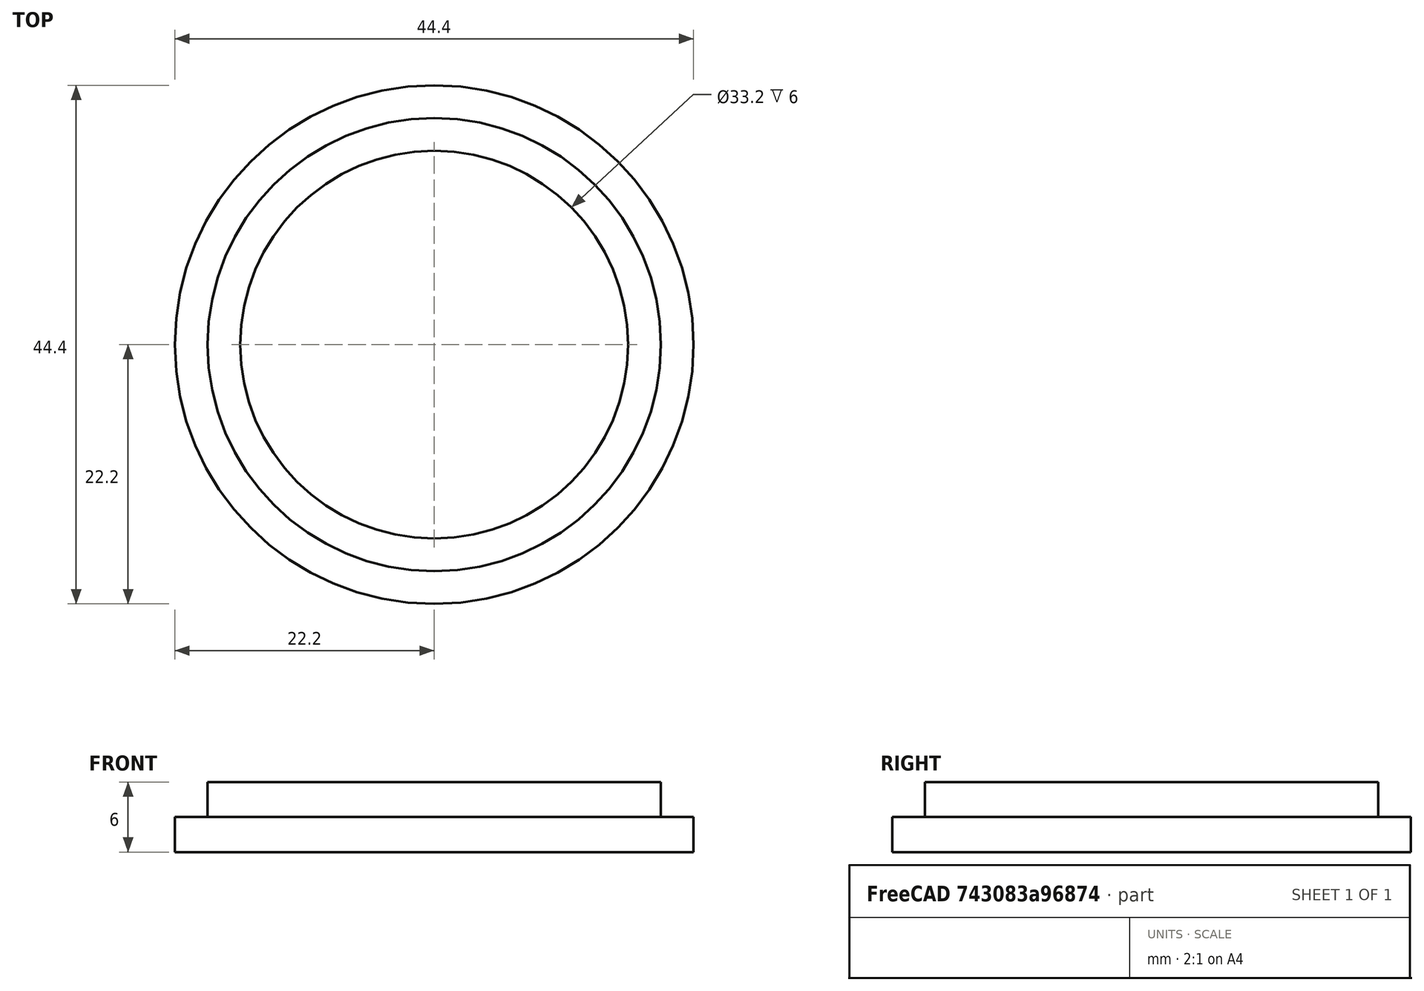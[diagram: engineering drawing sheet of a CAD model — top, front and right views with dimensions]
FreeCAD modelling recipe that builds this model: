
FCSTD DOCUMENT  (FreeCAD 0.19R24276 (Git))
Label: seal
License: All rights reserved
LicenseURL: http://en.wikipedia.org/wiki/All_rights_reserved
objects: Sketcher::SketchObject×1, PartDesign::Revolution×1, PartDesign::Body×1, App::Part×1, Mesh::Feature×1
note: 4 computed .brp shape members not serialized (recipe doc carries the construction recipe); baked Part::Feature solids carry a one-line shape summary decoded from their .brp

FEATURE [Sketcher::SketchObject] Sketch
  FullyConstrained = true
  MapMode = 5
  Placement = pos=(0,0,0) rot=(1,0,0;1.5708rad)
  Support = -> [XZ_Plane001]
  sketch-geometry (6):
    g0: LineSegment StartX=16.6 StartY=6 StartZ=0 EndX=16.6 EndY=0 EndZ=0
    g1: LineSegment StartX=16.6 StartY=0 StartZ=0 EndX=22.2 EndY=0 EndZ=0
    g2: LineSegment StartX=22.2 StartY=0 StartZ=0 EndX=22.2 EndY=3 EndZ=0
    g3: LineSegment StartX=22.2 StartY=3 StartZ=0 EndX=19.4 EndY=3 EndZ=0
    g4: LineSegment StartX=19.4 StartY=3 StartZ=0 EndX=19.4 EndY=6 EndZ=0
    g5: LineSegment StartX=19.4 StartY=6 StartZ=0 EndX=16.6 EndY=6 EndZ=0
  constraints (18):
    c: PointOnObject(g0,g-1)
    c: Vertical(g0)
    c: Coincident(g0,g1)
    c: Horizontal(g1)
    c: Coincident(g1,g2)
    c: Vertical(g2)
    c: Coincident(g2,g3)
    c: Horizontal(g3)
    c: Coincident(g3,g4)
    c: Vertical(g4)
    c: Coincident(g4,g5)
    c: Coincident(g5,g0)
    c: Horizontal(g5)
    c: DistanceX(g-1,g1) = 22.2
    c: DistanceY(g0,g0) = 6
    c: DistanceY(g2,g2) = 3
    c: DistanceX(g-1,g4) = 19.4
    c: Equal(g3,g5)
FEATURE [PartDesign::Revolution] Revolution
  Angle = 360
  Axis = (0,-2e-16,1)
  Base = (0,0,0)
  Placement = pos=(0,0,0) rot=(1,0,0;1.5708rad)
  Profile = -> Sketch
  ReferenceAxis = -> Sketch [V_Axis]
  Reversed = true
FEATURE [PartDesign::Body] Body
  Group = -> [Sketch,Revolution]
  Origin = -> Origin001
  Tip = -> Revolution
FEATURE [App::Part] Part
  Group = -> [Body]
  Origin = -> Origin
FEATURE [Mesh::Feature] Mesh  label="Body (Meshed)"
